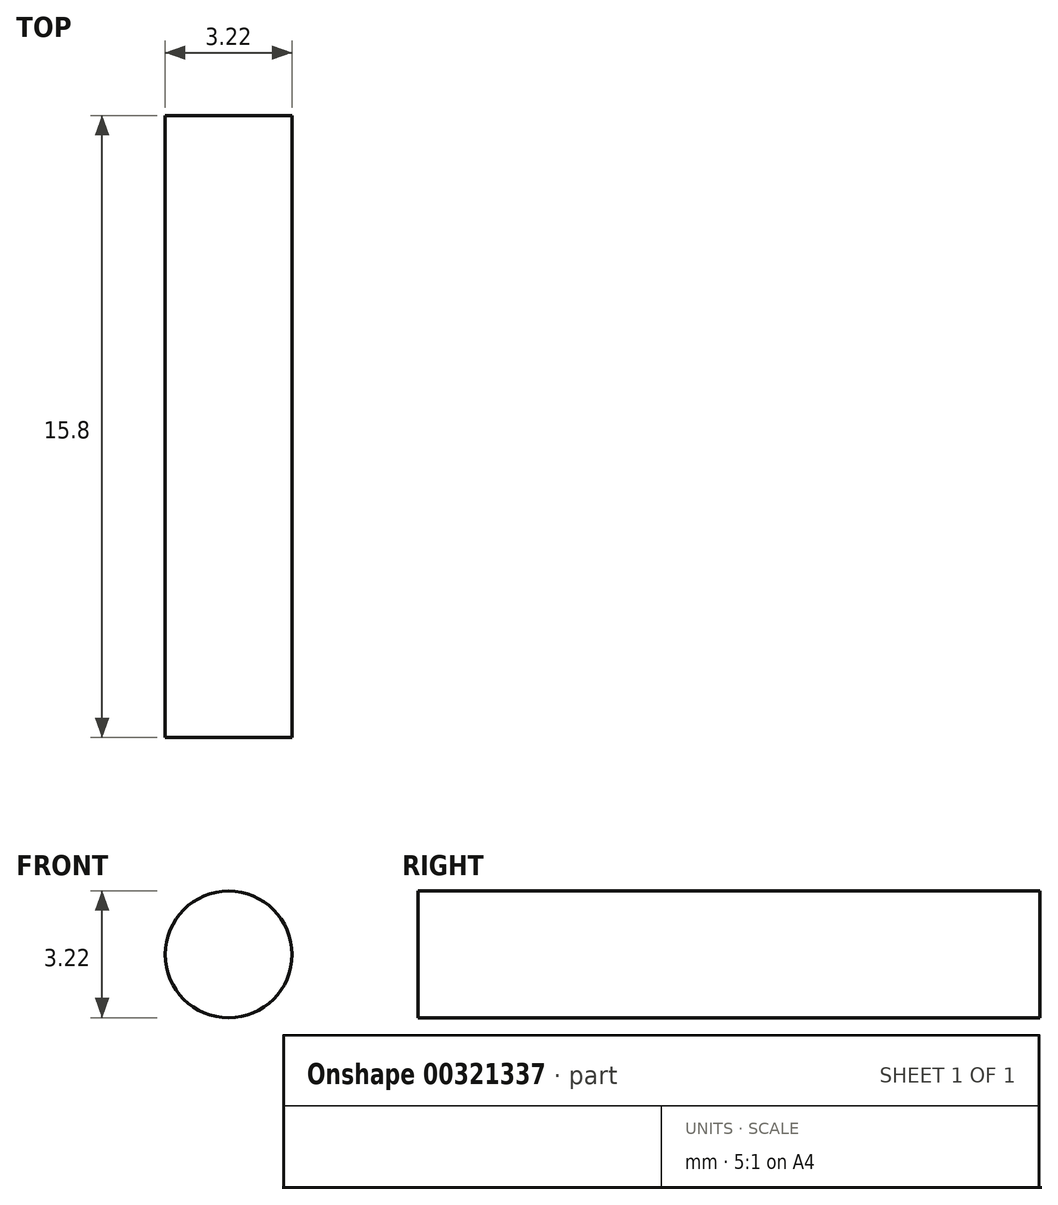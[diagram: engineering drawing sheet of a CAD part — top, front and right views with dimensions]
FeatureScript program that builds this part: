
annotation { "Feature Type Name" : "Feature", "Feature Type Description" : "" }
export const myFeature = defineFeature(function(context is Context, id is Id, definition is map)
    precondition{}
    {
        {
            var Q0;
            Q0=qCreatedBy(makeId("Front.planeOp"),FACE);
            var sketch = newSketch(context, id + "F0", { "sketchPlane" : qUnion([Q0])});
            skCircle(sketch, "E0", {"center": v(-24.95, 28.82) * mm, "radius": 1.61 * mm});
            skLineSegment(sketch, "E1", {"start": v(-26.56, 28.82) * mm, "end": v(-31.72, 18.26) * mm});
            skLineSegment(sketch, "E2", {"start": v(-31.72, 18.26) * mm, "end": v(-31.72, 15.07) * mm});
            skLineSegment(sketch, "E3", {"start": v(-31.72, 15.07) * mm, "end": v(-23.72, 15.07) * mm});
            skLineSegment(sketch, "E4", {"start": v(-23.72, 15.07) * mm, "end": v(-23.72, 27.77) * mm});
            skSolve(sketch);
        }
        {
            var Q0;
            {var subQ0=sQuery(id+"F0.wireOp",EDGE,"E0");var subQ1=makeQuery(id+"F0.imprint","INTERSECT",VERTEX,{"derivedFrom":[subQ0,sQuery(id+"F0.wireOp",EDGE,"E1")]});Q0=makeQuery(id+"F0.imprint","IMPRINT",FACE,{"disambiguationData":[TD([[makeQuery(id+"F0.imprint","IMPRINT",EDGE,{"disambiguationData":[TD([[subQ1,-1.0]])],"derivedFrom":subQ0}),1.0]])]});}
            extrude(context, id + "F1", {"entities" : qUnion([Q0]), "depth" : 15.8 * mm});
        }
    });
